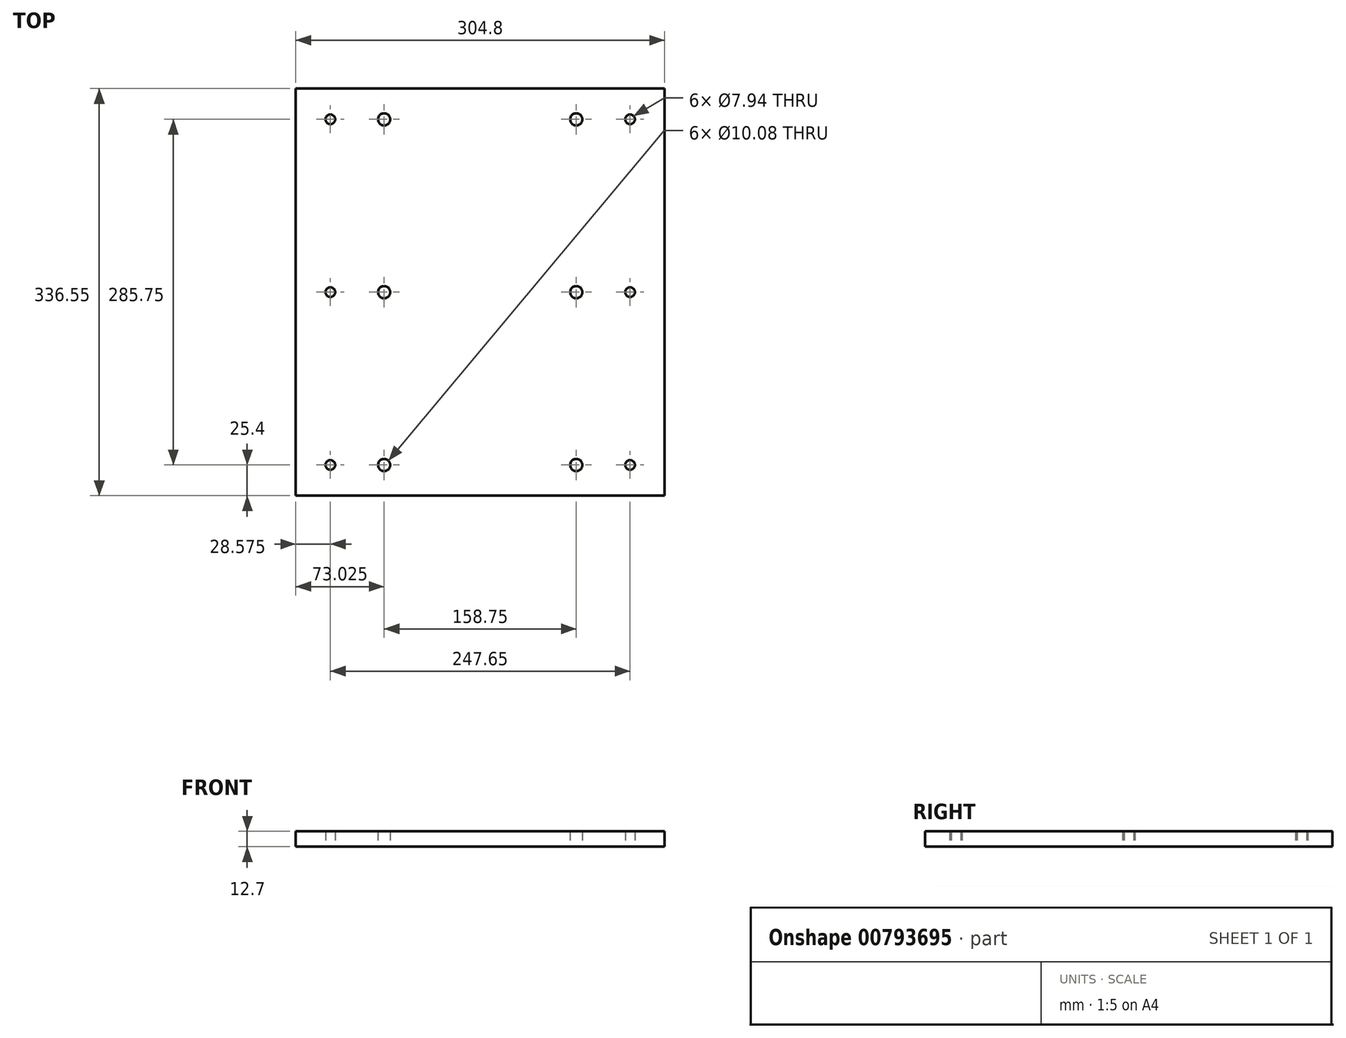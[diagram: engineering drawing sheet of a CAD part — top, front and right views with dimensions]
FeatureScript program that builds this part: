
annotation { "Feature Type Name" : "Feature", "Feature Type Description" : "" }
export const myFeature = defineFeature(function(context is Context, id is Id, definition is map)
    precondition{}
    {
        {
            var Q0;
            Q0=qCreatedBy(makeId("Top.planeOp"),FACE);
            var sketch = newSketch(context, id + "F0", { "sketchPlane" : qUnion([Q0])});
            skLineSegment(sketch, "E0.bottom", {"start": v(0, 0) * mm, "end": v(304.8, 0) * mm});
            skLineSegment(sketch, "E0.top", {"start": v(0, 336.55) * mm, "end": v(304.8, 336.55) * mm});
            skLineSegment(sketch, "E0.left", {"start": v(0, 0) * mm, "end": v(0, 336.55) * mm});
            skLineSegment(sketch, "E0.right", {"start": v(304.8, 0) * mm, "end": v(304.8, 336.55) * mm});
            skLineSegment(sketch, "E1", {"start": v(152.4, 336.55) * mm, "end": v(152.4, 0) * mm, "construction": true});
            skLineSegment(sketch, "E2", {"start": v(276.22, 336.55) * mm, "end": v(276.22, 0) * mm, "construction": true});
            skLineSegment(sketch, "E3", {"start": v(231.77, 336.55) * mm, "end": v(231.78, 0) * mm, "construction": true});
            skPoint(sketch, "E4", {"position": v(276.22, 311.15) * mm});
            skPoint(sketch, "E5", {"position": v(231.77, 311.15) * mm});
            skPoint(sketch, "E6", {"position": v(231.77, 168.28) * mm});
            skPoint(sketch, "E7", {"position": v(276.22, 168.28) * mm});
            skPoint(sketch, "E8", {"position": v(231.78, 25.4) * mm});
            skPoint(sketch, "E9", {"position": v(276.22, 25.4) * mm});
            skPoint(sketch, "E10.MirrorP", {"position": v(73.03, 168.28) * mm});
            skPoint(sketch, "E11.MirrorP", {"position": v(73.03, 311.15) * mm});
            skPoint(sketch, "E12.MirrorP", {"position": v(28.58, 311.15) * mm});
            skPoint(sketch, "E13.MirrorP", {"position": v(28.58, 168.28) * mm});
            skPoint(sketch, "E14.MirrorP", {"position": v(73.03, 25.4) * mm});
            skPoint(sketch, "E15.MirrorP", {"position": v(28.58, 25.4) * mm});
            skSolve(sketch);
        }
        {
            var Q0;
            Q0=makeQuery(id+"F0.imprint","IMPRINT",FACE,{"disambiguationData":[TD([[makeQuery(id+"F0.imprint","IMPRINT",EDGE,{"derivedFrom":sQuery(id+"F0.wireOp",EDGE,"E0.bottom")}),1.0]])]});
            extrude(context, id + "F1", {"entities" : qUnion([Q0]), "depth" : 12.7 * mm, "offsetDistance" : 25.4 * mm});
        }
        {
            var Q0;
            Q0=sQuery(id+"F0.wireOp",VERTEX,"E9");
            var Q1;
            Q1=sQuery(id+"F0.wireOp",VERTEX,"E4");
            var Q2;
            Q2=sQuery(id+"F0.wireOp",VERTEX,"E7");
            var Q3;
            Q3=sQuery(id+"F0.wireOp",VERTEX,"E13.MirrorP");
            var Q4;
            Q4=sQuery(id+"F0.wireOp",VERTEX,"E12.MirrorP");
            var Q5;
            Q5=sQuery(id+"F0.wireOp",VERTEX,"E15.MirrorP");
            var Q6;
            Q6=makeQuery(id+"F1.opExtrude","SWEPT_BODY",BODY,{"disambiguationData":[OSD([sQuery(id+"F0.wireOp",EDGE,"E0.bottom"),sQuery(id+"F0.wireOp",EDGE,"E0.top"),sQuery(id+"F0.wireOp",EDGE,"E0.left"),sQuery(id+"F0.wireOp",EDGE,"E0.right")])]});
            hole(context, id + "F2", {"style" : HoleStyle.SIMPLE, "endStyle" : HoleEndStyle.THROUGH, "oppositeDirection" : true, "standardTappedOrClearance" : lookupTablePath({ "fit" : "Normal (ASME)", "standard" : "ANSI", "engagement" : "75%", "pitch" : "16 tpi", "size" : "3/8", "type" : "Tapped" }), "standardBlindInLast" : lookupTablePath({ "fit" : "Free", "standard" : "ANSI", "engagement" : "75%", "pitch" : "16 tpi", "size" : "3/8", "type" : "Tapped" }), "holeDiameter" : 7.94 * mm, "majorDiameter" : 9.52 * mm, "showTappedDepth" : true, "isTappedThrough" : true, "tappedDepth" : 12.7 * mm, "tapClearance" : 3, "locations" : qUnion([Q0, Q1, Q2, Q3, Q4, Q5]), "scope" : qUnion([Q6])});
        }
        {
            var Q0;
            Q0=sQuery(id+"F0.wireOp",VERTEX,"E8");
            var Q1;
            Q1=sQuery(id+"F0.wireOp",VERTEX,"E6");
            var Q2;
            Q2=sQuery(id+"F0.wireOp",VERTEX,"E5");
            var Q3;
            Q3=sQuery(id+"F0.wireOp",VERTEX,"E11.MirrorP");
            var Q4;
            Q4=sQuery(id+"F0.wireOp",VERTEX,"E10.MirrorP");
            var Q5;
            Q5=sQuery(id+"F0.wireOp",VERTEX,"E14.MirrorP");
            var Q6;
            Q6=makeQuery(id+"F1.opExtrude","SWEPT_BODY",BODY,{"disambiguationData":[OSD([sQuery(id+"F0.wireOp",EDGE,"E0.bottom"),sQuery(id+"F0.wireOp",EDGE,"E0.top"),sQuery(id+"F0.wireOp",EDGE,"E0.left"),sQuery(id+"F0.wireOp",EDGE,"E0.right")])]});
            hole(context, id + "F3", {"style" : HoleStyle.SIMPLE, "endStyle" : HoleEndStyle.THROUGH, "oppositeDirection" : true, "standardTappedOrClearance" : lookupTablePath({ "fit" : "Normal (ASME)", "standard" : "ANSI", "size" : "3/8", "type" : "Clearance" }), "standardBlindInLast" : lookupTablePath({ "fit" : "Free", "standard" : "ANSI", "size" : "3/8", "type" : "Clearance" }), "holeDiameter" : 10.08 * mm, "majorDiameter" : 6.35 * mm, "isTappedThrough" : true, "tappedDepth" : 12.7 * mm, "tapClearance" : 3, "locations" : qUnion([Q0, Q1, Q2, Q3, Q4, Q5]), "scope" : qUnion([Q6])});
        }
    });
